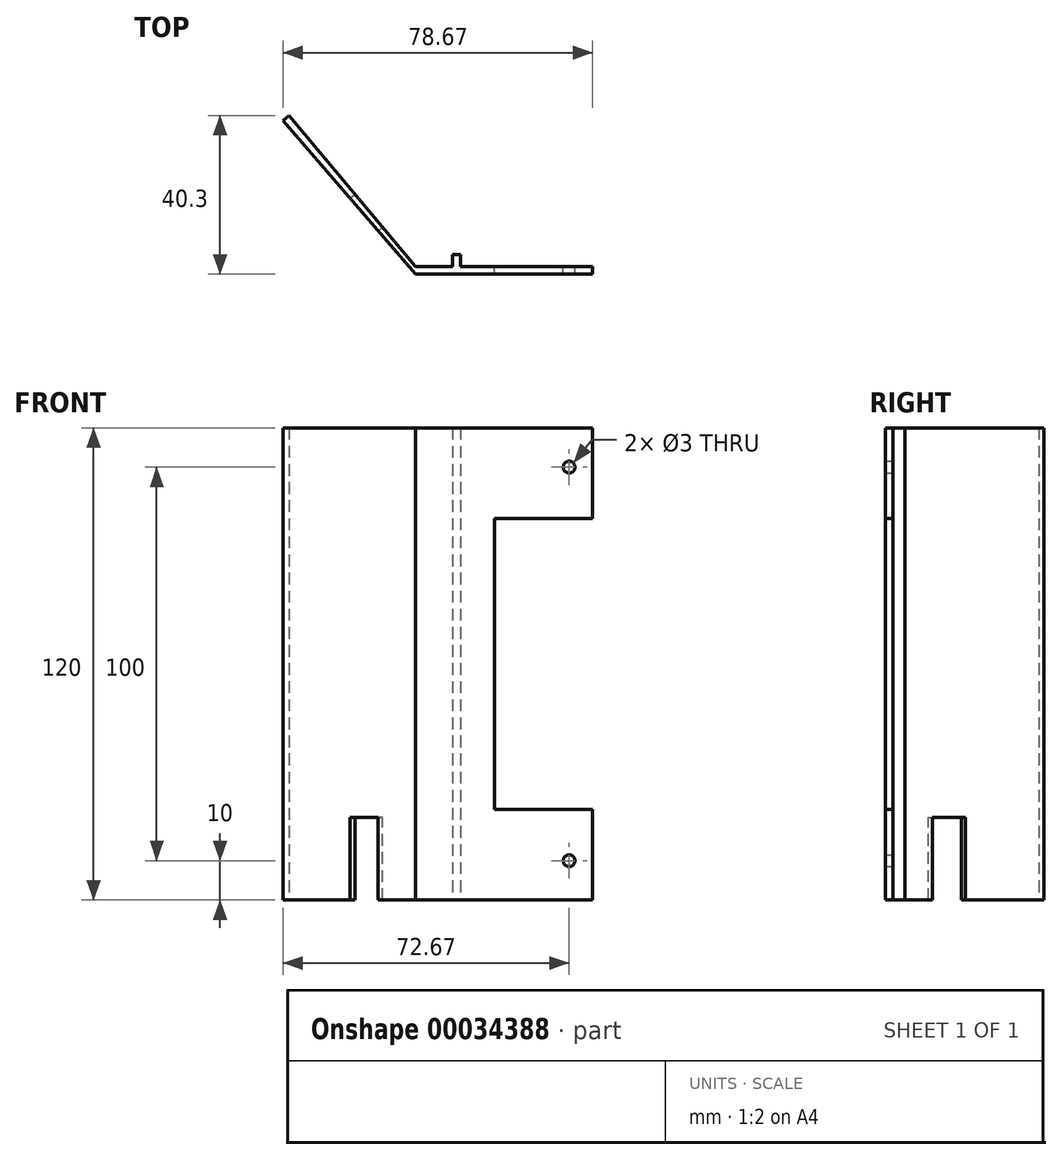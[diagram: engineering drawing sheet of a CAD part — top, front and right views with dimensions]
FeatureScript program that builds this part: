
annotation { "Feature Type Name" : "Feature", "Feature Type Description" : "" }
export const myFeature = defineFeature(function(context is Context, id is Id, definition is map)
    precondition{}
    {
        {
            var Q0;
            Q0=qCreatedBy(makeId("Top.planeOp"),FACE);
            var sketch = newSketch(context, id + "F0", { "sketchPlane" : qUnion([Q0])});
            skLineSegment(sketch, "E0", {"start": v(0, 0) * mm, "end": v(45, 0) * mm});
            skLineSegment(sketch, "E1", {"start": v(0, 0) * mm, "end": v(-32.14, 38.3) * mm});
            skLineSegment(sketch, "E2", {"start": v(45, 0) * mm, "end": v(45, -2) * mm});
            skLineSegment(sketch, "E3", {"start": v(45, -2) * mm, "end": v(0, -2) * mm});
            skLineSegment(sketch, "E4", {"start": v(-32.14, 38.3) * mm, "end": v(-33.67, 37.02) * mm});
            skLineSegment(sketch, "E5", {"start": v(-33.67, 37.02) * mm, "end": v(0, -2) * mm});
            skSolve(sketch);
        }
        {
            var Q0;
            Q0 = qSketchRegion(id + "F0", true);
            extrude(context, id + "F1", {"entities" : qUnion([Q0]), "depth" : 120 * mm});
        }
        {
            var Q0;
            Q0=makeQuery(id+"F1.opExtrude","SWEPT_FACE",FACE,{"disambiguationData":[OSD([sQuery(id+"F0.wireOp",EDGE,"E0")])]});
            var sketch = newSketch(context, id + "F6", { "sketchPlane" : qUnion([Q0])});
            skCircle(sketch, "E6", {"center": v(-39, 110) * mm, "radius": 1.5 * mm});
            skCircle(sketch, "E7", {"center": v(-39, 10) * mm, "radius": 3 * mm});
            skCircle(sketch, "E8", {"center": v(-39, 10) * mm, "radius": 1.5 * mm});
            skCircle(sketch, "E9", {"center": v(-39, 110) * mm, "radius": 3 * mm});
            skLineSegment(sketch, "E10.bottom", {"start": v(-45, 97) * mm, "end": v(-20, 97) * mm});
            skLineSegment(sketch, "E10.top", {"start": v(-45, 23) * mm, "end": v(-20, 23) * mm});
            skLineSegment(sketch, "E10.left", {"start": v(-45, 97) * mm, "end": v(-45, 23) * mm});
            skLineSegment(sketch, "E10.right", {"start": v(-20, 97) * mm, "end": v(-20, 23) * mm});
            skLineSegment(sketch, "E11.bottom", {"start": v(-11.4, 120) * mm, "end": v(-9.4, 120) * mm});
            skLineSegment(sketch, "E11.top", {"start": v(-11.4, 0) * mm, "end": v(-9.4, 0) * mm});
            skLineSegment(sketch, "E11.left", {"start": v(-11.4, 120) * mm, "end": v(-11.4, 0) * mm});
            skLineSegment(sketch, "E11.right", {"start": v(-9.4, 120) * mm, "end": v(-9.4, 0) * mm});
            skSolve(sketch);
        }
        {
            var Q0;
            Q0=makeQuery(id+"F6.imprint","IMPRINT",FACE,{"disambiguationData":[TD([[makeQuery(id+"F6.imprint","IMPRINT",EDGE,{"derivedFrom":sQuery(id+"F6.wireOp",EDGE,"E6")}),1.0]])]});
            var Q1;
            Q1=makeQuery(id+"F6.imprint","IMPRINT",FACE,{"disambiguationData":[TD([[makeQuery(id+"F6.imprint","IMPRINT",EDGE,{"derivedFrom":sQuery(id+"F6.wireOp",EDGE,"E8")}),1.0]])]});
            var Q2;
            Q2=makeQuery(id+"F6.imprint","IMPRINT",FACE,{"disambiguationData":[TD([[makeQuery(id+"F6.imprint","IMPRINT",EDGE,{"derivedFrom":sQuery(id+"F6.wireOp",EDGE,"E10.bottom")}),-1.0]])]});
            extrude(context, id + "F2", {"entities" : qUnion([Q0, Q1, Q2]), "operationType" : NewBodyOperationType.REMOVE, "endBound" : BoundingType.THROUGH_ALL, "oppositeDirection" : true, "depth" : 25 * mm});
        }
        {
            var Q0;
            Q0=makeQuery(id+"F6.imprint","IMPRINT",FACE,{"disambiguationData":[TD([[makeQuery(id+"F6.imprint","IMPRINT",EDGE,{"derivedFrom":sQuery(id+"F6.wireOp",EDGE,"E11.bottom")}),1.0]])]});
            extrude(context, id + "F3", {"entities" : qUnion([Q0]), "operationType" : NewBodyOperationType.ADD, "depth" : 3 * mm});
        }
        {
            var Q0;
            Q0=makeQuery(id+"F1.opExtrude","SWEPT_FACE",FACE,{"disambiguationData":[OSD([sQuery(id+"F0.wireOp",EDGE,"E1")])]});
            var sketch = newSketch(context, id + "F4", { "sketchPlane" : qUnion([Q0])});
            skLineSegment(sketch, "E12.bottom", {"start": v(13, 0) * mm, "end": v(24, 0) * mm});
            skLineSegment(sketch, "E12.top", {"start": v(13, 21) * mm, "end": v(24, 21) * mm});
            skLineSegment(sketch, "E12.left", {"start": v(13, 0) * mm, "end": v(13, 21) * mm});
            skLineSegment(sketch, "E12.right", {"start": v(24, 0) * mm, "end": v(24, 21) * mm});
            skSolve(sketch);
        }
        {
            var Q0;
            Q0=makeQuery(id+"F4.imprint","IMPRINT",FACE,{"disambiguationData":[TD([[makeQuery(id+"F4.imprint","IMPRINT",EDGE,{"derivedFrom":sQuery(id+"F4.wireOp",EDGE,"E12.bottom")}),1.0]])]});
            extrude(context, id + "F5", {"entities" : qUnion([Q0]), "operationType" : NewBodyOperationType.REMOVE, "oppositeDirection" : true, "depth" : 25 * mm});
        }
    });
